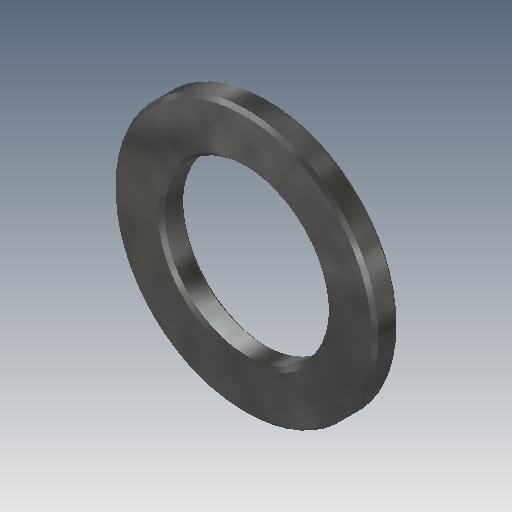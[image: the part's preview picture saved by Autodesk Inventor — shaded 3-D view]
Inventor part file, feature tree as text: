
AUTODESK INVENTOR PART (.ipt)
format: ipt  version: 2018 (Build 220112000, 112)  size: 139,264 bytes
history: native  units: mm
features: extrude x1, chamfer x1, sketch x1
ambient origin geometry x8: Origin, YZ Plane, XZ Plane, XY Plane, X Axis, Y Axis, Z Axis, Center Point
bodies: Solid1 (feature_tree)
feature tree (3):
  extrude  "Extrusion1"  Depth=1.5mm
  chamfer  "Chamfer1"  Distance=1.5mm
  sketch  "Sketch1"  dims[d0=10.0mm d1=16.0mm d2=1.5mm d3=0.0mm d4=0.2mm d5=2.0mm d6=45.0deg]
